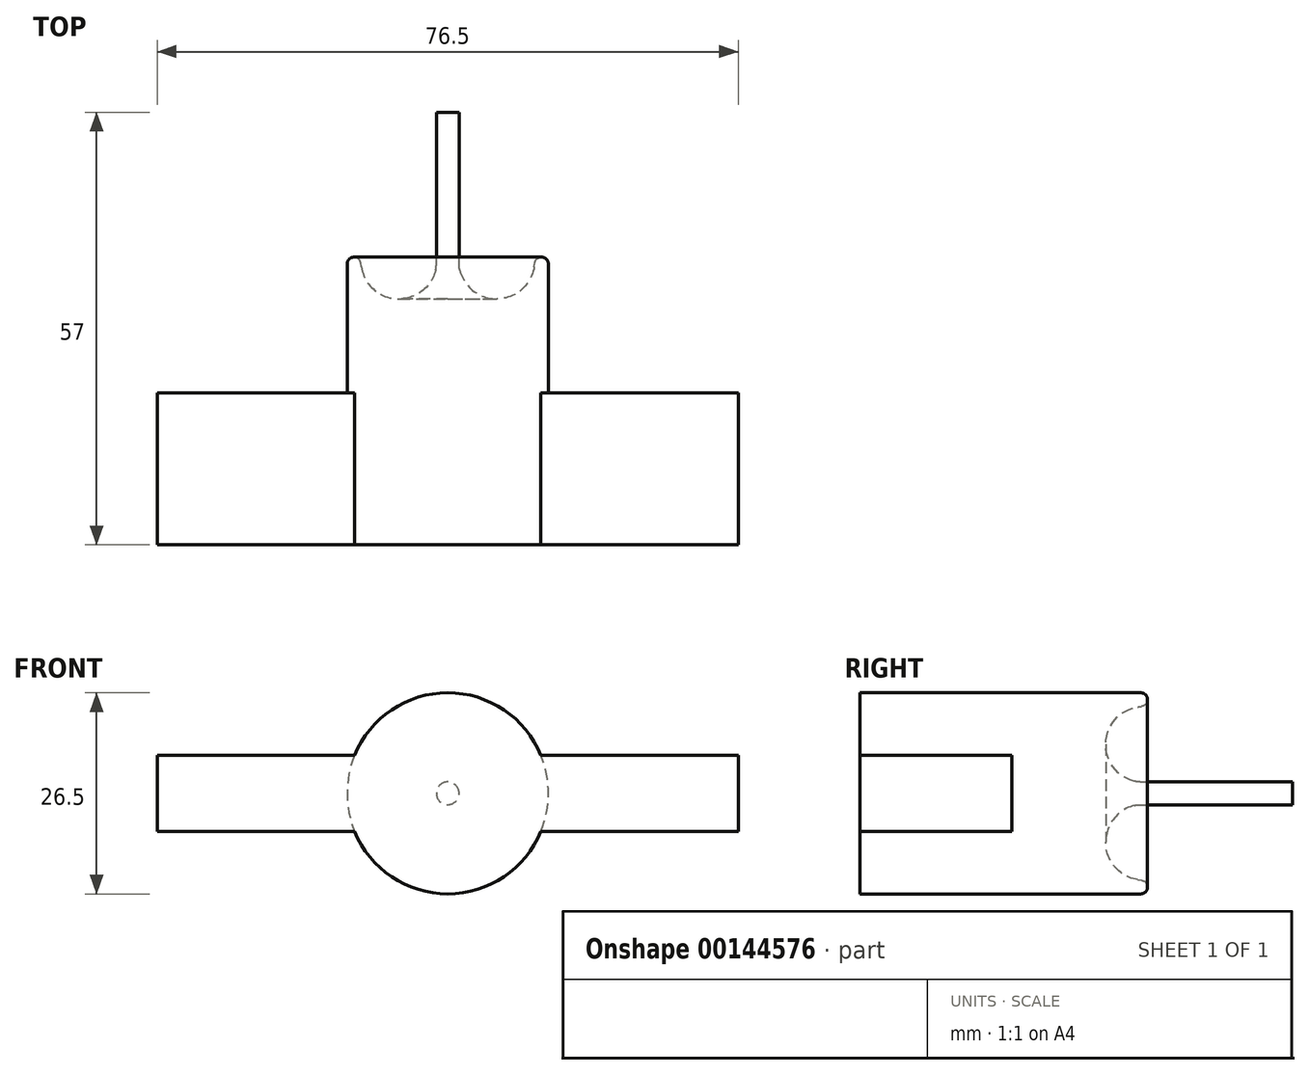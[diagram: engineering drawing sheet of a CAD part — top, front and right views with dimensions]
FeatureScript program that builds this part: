
annotation { "Feature Type Name" : "Feature", "Feature Type Description" : "" }
export const myFeature = defineFeature(function(context is Context, id is Id, definition is map)
    precondition{}
    {
        {
            var Q0;
            Q0=qCreatedBy(makeId("Top.planeOp"),FACE);
            var sketch = newSketch(context, id + "F0", { "sketchPlane" : qUnion([Q0])});
            skLineSegment(sketch, "E0", {"start": v(0, 0) * mm, "end": v(0, 8.99) * mm, "construction": true});
            skLineSegment(sketch, "E1", {"start": v(0, 0) * mm, "end": v(-13.25, 0) * mm});
            skLineSegment(sketch, "E2", {"start": v(-13.25, 0) * mm, "end": v(-13.25, 17) * mm});
            skArc(sketch, "E3", {"start": v(-11.38, 16.62) * mm, "mid": v(-6.44, 12.4) * mm, "end": v(-1.5, 16.62) * mm});
            skLineSegment(sketch, "E4", {"start": v(-1.5, 16.62) * mm, "end": v(-1.5, 37) * mm});
            skLineSegment(sketch, "E5", {"start": v(-1.5, 37) * mm, "end": v(0, 37) * mm});
            skLineSegment(sketch, "E6", {"start": v(0, 37) * mm, "end": v(0, 0) * mm});
            skArc(sketch, "E7", {"start": v(-11.46, 17.14) * mm, "mid": v(-12.42, 17.9) * mm, "end": v(-13.25, 17) * mm});
            skFitSpline(sketch, "E8", {"points": [v(-11.46, 17.14) * mm, v(-9.43, 12.3) * mm, v(-3.18, 12.17) * mm, v(-1.5, 16.62) * mm], "startDerivative": vector(0.25, -6.28) * mm, "endDerivative": vector(0.05, 11) * mm, "construction": true});
            skLineSegment(sketch, "E9", {"start": v(-11.46, 17.14) * mm, "end": v(-11.38, 16.62) * mm});
            skSolve(sketch);
        }
        {
            var Q0;
            Q0=makeQuery(id+"F0.imprint","IMPRINT",FACE,{"disambiguationData":[TD([[makeQuery(id+"F0.imprint","IMPRINT",EDGE,{"derivedFrom":sQuery(id+"F0.wireOp",EDGE,"E1")}),-1.0]])]});
            var Q1;
            Q1=sQuery(id+"F0.wireOp",EDGE,"E6");
            revolve(context, id + "F1", {"entities" : qUnion([Q0]), "axis" : qUnion([Q1]), "revolveType" : RevolveType.FULL});
        }
        {
            var Q0;
            Q0=makeQuery(id+"F1.opRevolve","SWEPT_EDGE",EDGE,{"disambiguationData":[OSD([sQuery(id+"F0.wireOp",EDGE,"E3"),sQuery(id+"F0.wireOp",EDGE,"E4")])]});
            fillet(context, id + "F2", {"entities" : qUnion([Q0]), "radius" : 3 * mm, "tangentPropagation" : true, "allowEdgeOverflow" : false});
        }
        {
            var Q0;
            Q0=makeQuery(id+"F1.opRevolve","SWEPT_FACE",FACE,{"disambiguationData":[OSD([sQuery(id+"F0.wireOp",EDGE,"E1")])]});
            var sketch = newSketch(context, id + "F3", { "sketchPlane" : qUnion([Q0])});
            skLineSegment(sketch, "E10.bottom", {"start": v(-38.25, 5) * mm, "end": v(38.25, 5) * mm});
            skLineSegment(sketch, "E10.top", {"start": v(-38.25, -5) * mm, "end": v(38.25, -5) * mm});
            skLineSegment(sketch, "E10.left", {"start": v(-38.25, 5) * mm, "end": v(-38.25, -5) * mm});
            skLineSegment(sketch, "E10.right", {"start": v(38.25, 5) * mm, "end": v(38.25, -5) * mm});
            skLineSegment(sketch, "E11", {"start": v(0, 0) * mm, "end": v(13.25, 0) * mm});
            skLineSegment(sketch, "E12", {"start": v(0, 0) * mm, "end": v(0, -3.36) * mm});
            skSolve(sketch);
        }
        {
            var Q0;
            {var subQ0=sQuery(id+"F3.wireOp",EDGE,"E10.left");Q0=makeQuery(id+"F3.imprint","IMPRINT",FACE,{"disambiguationData":[TD([[makeQuery(id+"F3.imprint","IMPRINT",EDGE,{"derivedFrom":subQ0}),1.0]])]});}
            var Q1;
            {var subQ4=sQuery(id+"F3.wireOp",EDGE,"E10.right");Q1=makeQuery(id+"F3.imprint","IMPRINT",FACE,{"disambiguationData":[TD([[makeQuery(id+"F3.imprint","IMPRINT",EDGE,{"derivedFrom":subQ4}),-1.0]])]});}
            var Q2;
            {var subQ0=makeQuery(id+"F1.opRevolve","SWEPT_EDGE",EDGE,{"disambiguationData":[OSD([sQuery(id+"F0.wireOp",EDGE,"E1"),sQuery(id+"F0.wireOp",EDGE,"E2")])]});var subQ3=makeQuery(id+"F3.imprint","IMPRINT",VERTEX,{"derivedFrom":subQ0});Q2=makeQuery(id+"F3.imprint","IMPRINT",FACE,{"disambiguationData":[TD([[makeQuery(id+"F3.imprint","IMPRINT",EDGE,{"disambiguationData":[TD([[subQ3,1.0]])],"derivedFrom":subQ0}),-1.0]])]});}
            extrude(context, id + "F4", {"entities" : qUnion([Q0, Q1, Q2]), "operationType" : NewBodyOperationType.ADD, "depth" : 20 * mm});
        }
        {
            var Q0;
            {var subQ0=sQuery(id+"F3.wireOp",EDGE,"E10.bottom");Q0=makeQuery(id+"F4.boolean.opBoolean","SPLIT",FACE,{"disambiguationData":[TD([makeQuery(id+"F4.opExtrude","SWEPT_FACE",FACE,{"disambiguationData":[OSD([subQ0])]})])],"derivedFrom":makeQuery(id+"F1.opRevolve","SWEPT_FACE",FACE,{"disambiguationData":[OSD([sQuery(id+"F0.wireOp",EDGE,"E1")])]})});}
            var Q1;
            {var subQ0=sQuery(id+"F3.wireOp",EDGE,"E10.top");Q1=makeQuery(id+"F4.boolean.opBoolean","SPLIT",FACE,{"disambiguationData":[TD([makeQuery(id+"F4.opExtrude","SWEPT_FACE",FACE,{"disambiguationData":[OSD([subQ0])]})])],"derivedFrom":makeQuery(id+"F1.opRevolve","SWEPT_FACE",FACE,{"disambiguationData":[OSD([sQuery(id+"F0.wireOp",EDGE,"E1")])]})});}
            extrude(context, id + "F5", {"entities" : qUnion([Q0, Q1]), "operationType" : NewBodyOperationType.ADD, "depth" : 20 * mm});
        }
    });
